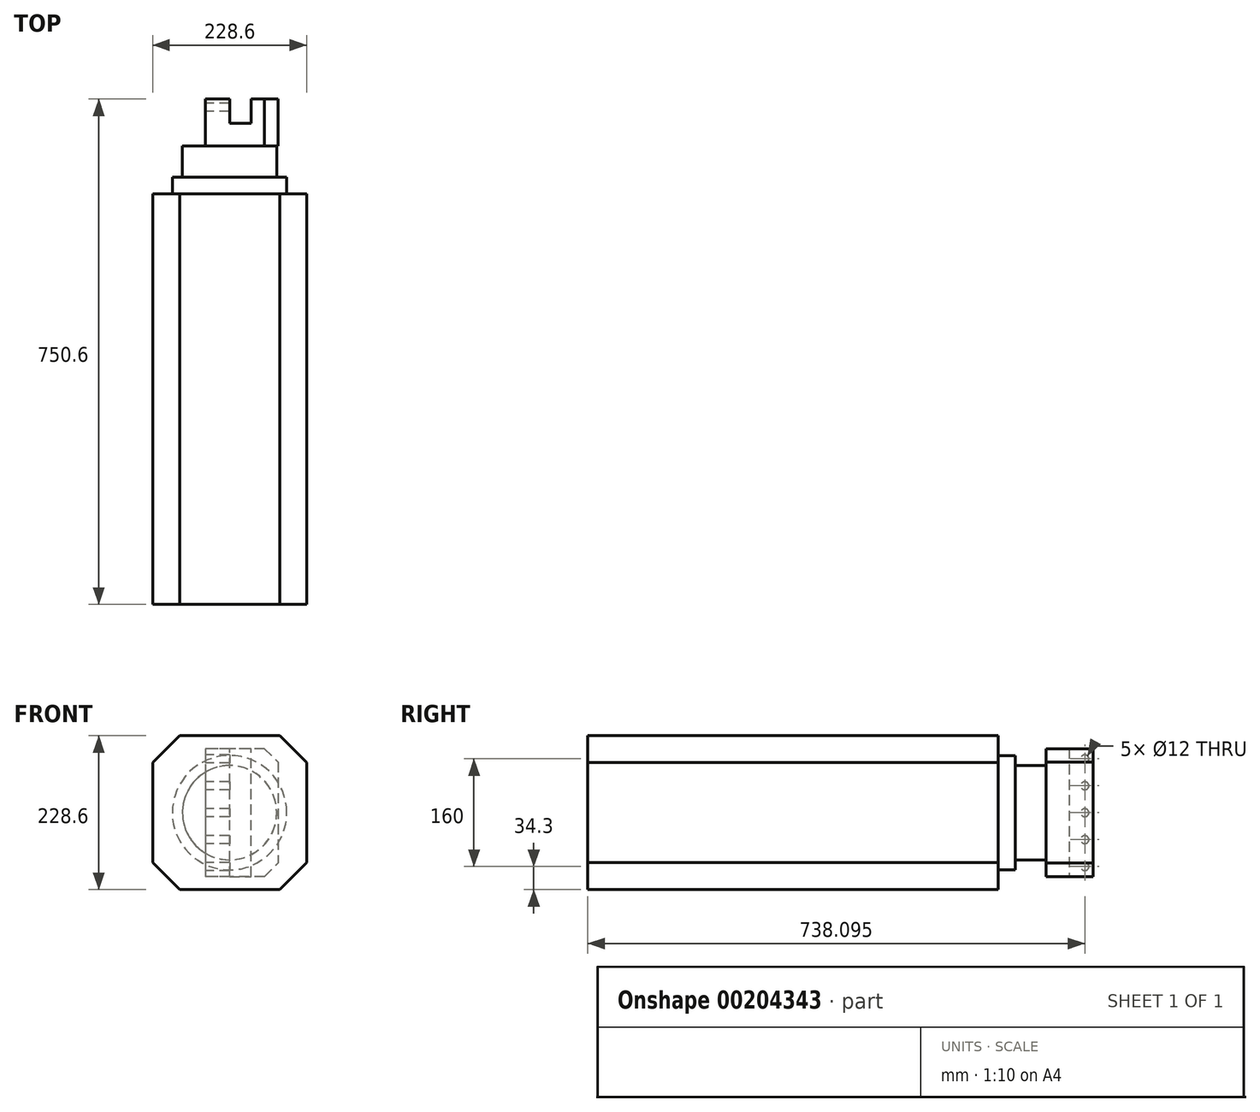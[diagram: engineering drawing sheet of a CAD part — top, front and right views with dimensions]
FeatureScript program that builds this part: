
annotation { "Feature Type Name" : "Feature", "Feature Type Description" : "" }
export const myFeature = defineFeature(function(context is Context, id is Id, definition is map)
    precondition{}
    {
        {
            var Q0;
            Q0=qCreatedBy(makeId("Front.planeOp"),FACE);
            var sketch = newSketch(context, id + "F0", { "sketchPlane" : qUnion([Q0])});
            skLineSegment(sketch, "E0.bottom", {"start": v(-114.3, -114.3) * mm, "end": v(114.3, -114.3) * mm});
            skLineSegment(sketch, "E0.top", {"start": v(-114.3, 114.3) * mm, "end": v(114.3, 114.3) * mm});
            skLineSegment(sketch, "E0.left", {"start": v(-114.3, -114.3) * mm, "end": v(-114.3, 114.3) * mm});
            skLineSegment(sketch, "E0.right", {"start": v(114.3, -114.3) * mm, "end": v(114.3, 114.3) * mm});
            skPoint(sketch, "E0.middle", {"position": v(0, 0) * mm});
            skSolve(sketch);
        }
        {
            var Q0;
            Q0 = qSketchRegion(id + "F0", true);
            extrude(context, id + "F1", {"entities" : qUnion([Q0]), "depth" : 609.6 * mm});
        }
        {
            var Q0;
            Q0=qCreatedBy(makeId("Top.planeOp"),FACE);
            var sketch = newSketch(context, id + "F2", { "sketchPlane" : qUnion([Q0])});
            skLineSegment(sketch, "E1.bottom", {"start": v(114.3, 89.93) * mm, "end": v(-114.3, 89.93) * mm});
            skLineSegment(sketch, "E1.top", {"start": v(114.3, -62.47) * mm, "end": v(-114.3, -62.47) * mm});
            skLineSegment(sketch, "E1.left", {"start": v(114.3, 89.93) * mm, "end": v(114.3, -62.47) * mm});
            skLineSegment(sketch, "E1.right", {"start": v(-114.3, 89.93) * mm, "end": v(-114.3, -62.47) * mm});
            skPoint(sketch, "E1.middle", {"position": v(0, 13.73) * mm});
            skSolve(sketch);
        }
        {
            var Q0;
            Q0=makeQuery(id+"F1.opExtrude","SWEPT_EDGE",EDGE,{"disambiguationData":[OSD([sQuery(id+"F0.wireOp",EDGE,"E0.top"),sQuery(id+"F0.wireOp",EDGE,"E0.right")])]});
            var Q1;
            Q1=makeQuery(id+"F1.opExtrude","SWEPT_EDGE",EDGE,{"disambiguationData":[OSD([sQuery(id+"F0.wireOp",EDGE,"E0.top"),sQuery(id+"F0.wireOp",EDGE,"E0.left")])]});
            var Q2;
            Q2=makeQuery(id+"F1.opExtrude","SWEPT_EDGE",EDGE,{"disambiguationData":[OSD([sQuery(id+"F0.wireOp",EDGE,"E0.bottom"),sQuery(id+"F0.wireOp",EDGE,"E0.left")])]});
            var Q3;
            Q3=makeQuery(id+"F1.opExtrude","SWEPT_EDGE",EDGE,{"disambiguationData":[OSD([sQuery(id+"F0.wireOp",EDGE,"E0.bottom"),sQuery(id+"F0.wireOp",EDGE,"E0.right")])]});
            chamfer(context, id + "F3", {"entities" : qUnion([Q0, Q1, Q2, Q3]), "width" : 40 * mm, "tangentPropagation" : true});
        }
        {
            var Q0;
            Q0=qCreatedBy(makeId("Front.planeOp"),FACE);
            var sketch = newSketch(context, id + "F4", { "sketchPlane" : qUnion([Q0])});
            skCircle(sketch, "E2", {"center": v(0, 0) * mm, "radius": 85 * mm});
            skSolve(sketch);
        }
        {
            var Q0;
            Q0 = qSketchRegion(id + "F4", true);
            extrude(context, id + "F5", {"entities" : qUnion([Q0]), "operationType" : NewBodyOperationType.ADD, "oppositeDirection" : true, "depth" : 25 * mm});
        }
        {
            var Q0;
            Q0=makeQuery(id+"F5.opExtrude","CAP_FACE",FACE,{"disambiguationData":[OSD([sQuery(id+"F4.wireOp",EDGE,"E2")])],"isStart":false});
            var sketch = newSketch(context, id + "F6", { "sketchPlane" : qUnion([Q0])});
            skCircle(sketch, "E3", {"center": v(0, 0) * mm, "radius": 70 * mm});
            skSolve(sketch);
        }
        {
            var Q0;
            Q0 = qSketchRegion(id + "F6", true);
            extrude(context, id + "F7", {"entities" : qUnion([Q0]), "operationType" : NewBodyOperationType.ADD, "depth" : 46 * mm});
        }
        {
            var Q0;
            Q0=makeQuery(id+"F7.opExtrude","CAP_FACE",FACE,{"disambiguationData":[OSD([sQuery(id+"F6.wireOp",EDGE,"E3")])],"isStart":false});
            var sketch = newSketch(context, id + "F8", { "sketchPlane" : qUnion([Q0])});
            skLineSegment(sketch, "E4.bottom", {"start": v(-72, 95) * mm, "end": v(36, 95) * mm});
            skLineSegment(sketch, "E4.top", {"start": v(-72, -95) * mm, "end": v(36, -95) * mm});
            skLineSegment(sketch, "E4.left", {"start": v(-72, 95) * mm, "end": v(-72, -95) * mm});
            skPoint(sketch, "E4.middle", {"position": v(0, 0) * mm});
            skLineSegment(sketch, "E5", {"start": v(0, 0) * mm, "end": v(0, -95) * mm});
            skLineSegment(sketch, "E6", {"start": v(0, 0) * mm, "end": v(0, 95) * mm});
            skPoint(sketch, "E6.endSnap0", {"position": v(0, 95) * mm});
            skLineSegment(sketch, "E7.0", {"start": v(-32, 0) * mm, "end": v(-32, -95) * mm});
            skLineSegment(sketch, "E7.1", {"start": v(-32, 0) * mm, "end": v(-32, 95) * mm});
            skLineSegment(sketch, "E8.0", {"start": v(-75.61, 117.47) * mm, "end": v(-117.47, 75.61) * mm});
            skLineSegment(sketch, "E8.2", {"start": v(-117.47, 75.61) * mm, "end": v(-117.47, -75.61) * mm});
            skLineSegment(sketch, "E8.3", {"start": v(117.47, 75.61) * mm, "end": v(75.61, 117.47) * mm});
            skLineSegment(sketch, "E8.4", {"start": v(-117.47, -75.61) * mm, "end": v(-75.61, -117.47) * mm});
            skLineSegment(sketch, "E8.5", {"start": v(-75.61, -117.47) * mm, "end": v(75.61, -117.47) * mm});
            skLineSegment(sketch, "E8.6", {"start": v(75.61, -117.47) * mm, "end": v(117.47, -75.61) * mm});
            skLineSegment(sketch, "E8.7", {"start": v(117.47, -75.61) * mm, "end": v(117.47, 75.61) * mm});
            skLineSegment(sketch, "E9", {"start": v(36, 95) * mm, "end": v(36, -95) * mm});
            skPoint(sketch, "E4.right.start.orphan", {"position": v(72, 95) * mm});
            skPoint(sketch, "E10.orphan", {"position": v(72, -95) * mm});
            skPoint(sketch, "E11.trimOffspring.end.orphan", {"position": v(0, 136.1) * mm});
            skSolve(sketch);
        }
        {
            var Q0;
            Q0 = qSketchRegion(id + "F8", true);
            extrude(context, id + "F9", {"entities" : qUnion([Q0]), "operationType" : NewBodyOperationType.ADD, "depth" : 70 * mm});
        }
        {
            var Q0;
            Q0=makeQuery(id+"F9.opExtrude","SWEPT_FACE",FACE,{"disambiguationData":[OSD([sQuery(id+"F8.wireOp",EDGE,"E4.top")])]});
            var sketch = newSketch(context, id + "F10", { "sketchPlane" : qUnion([Q0])});
            skLineSegment(sketch, "E12", {"start": v(0, -105) * mm, "end": v(0, -150.42) * mm});
            skLineSegment(sketch, "E13.0", {"start": v(32, -105) * mm, "end": v(32, -150.42) * mm});
            skLineSegment(sketch, "E14", {"start": v(0, -105) * mm, "end": v(32, -105) * mm});
            skPoint(sketch, "E15.orphan", {"position": v(0, -71) * mm});
            skLineSegment(sketch, "E16", {"start": v(0, -150.42) * mm, "end": v(32, -150.42) * mm});
            skSolve(sketch);
        }
        {
            var Q0;
            Q0 = qSketchRegion(id + "F10", true);
            extrude(context, id + "F11", {"entities" : qUnion([Q0]), "operationType" : NewBodyOperationType.REMOVE, "oppositeDirection" : true, "depth" : 252 * mm});
        }
        {
            var Q0;
            Q0=makeQuery(id+"F9.opExtrude","SWEPT_EDGE",EDGE,{"disambiguationData":[OSD([sQuery(id+"F8.wireOp",EDGE,"E4.top"),sQuery(id+"F8.wireOp",EDGE,"E4.left")])]});
            var Q1;
            Q1=makeQuery(id+"F9.opExtrude","SWEPT_EDGE",EDGE,{"disambiguationData":[OSD([sQuery(id+"F8.wireOp",EDGE,"E4.bottom"),sQuery(id+"F8.wireOp",EDGE,"E4.left")])]});
            chamfer(context, id + "F12", {"entities" : qUnion([Q0, Q1]), "width" : 20 * mm, "tangentPropagation" : true});
        }
        {
            var Q0;
            Q0=makeQuery(id+"F9.opExtrude","SWEPT_FACE",FACE,{"disambiguationData":[OSD([sQuery(id+"F8.wireOp",EDGE,"E9")])]});
            var sketch = newSketch(context, id + "F13", { "sketchPlane" : qUnion([Q0])});
            skPoint(sketch, "E17", {"position": v(-128.5, 80) * mm});
            skPoint(sketch, "E18", {"position": v(-128.5, 40) * mm});
            skPoint(sketch, "E19", {"position": v(-128.5, 0) * mm});
            skPoint(sketch, "E20", {"position": v(-128.5, -40) * mm});
            skPoint(sketch, "E21", {"position": v(-128.5, -80) * mm});
            skSolve(sketch);
        }
        {
            var Q0;
            Q0=sQuery(id+"F13.wireOp",VERTEX,"E17");
            var Q1;
            Q1=sQuery(id+"F13.wireOp",VERTEX,"E18");
            var Q2;
            Q2=sQuery(id+"F13.wireOp",VERTEX,"E19");
            var Q3;
            Q3=sQuery(id+"F13.wireOp",VERTEX,"E20");
            var Q4;
            Q4=sQuery(id+"F13.wireOp",VERTEX,"E21");
            var Q5;
            Q5=makeQuery(id+"F1.opExtrude","SWEPT_BODY",BODY,{"disambiguationData":[OSD([sQuery(id+"F0.wireOp",EDGE,"E0.bottom"),sQuery(id+"F0.wireOp",EDGE,"E0.top"),sQuery(id+"F0.wireOp",EDGE,"E0.left"),sQuery(id+"F0.wireOp",EDGE,"E0.right")])]});
            hole(context, id + "F14", {"style" : HoleStyle.SIMPLE, "endStyle" : HoleEndStyle.BLIND, "holeDiameter" : 12 * mm, "holeDepth" : 40 * mm, "isTappedThrough" : true, "tappedDepth" : 12 * mm, "tapClearance" : 3, "locations" : qUnion([Q0, Q1, Q2, Q3, Q4]), "scope" : qUnion([Q5])});
        }
    });
